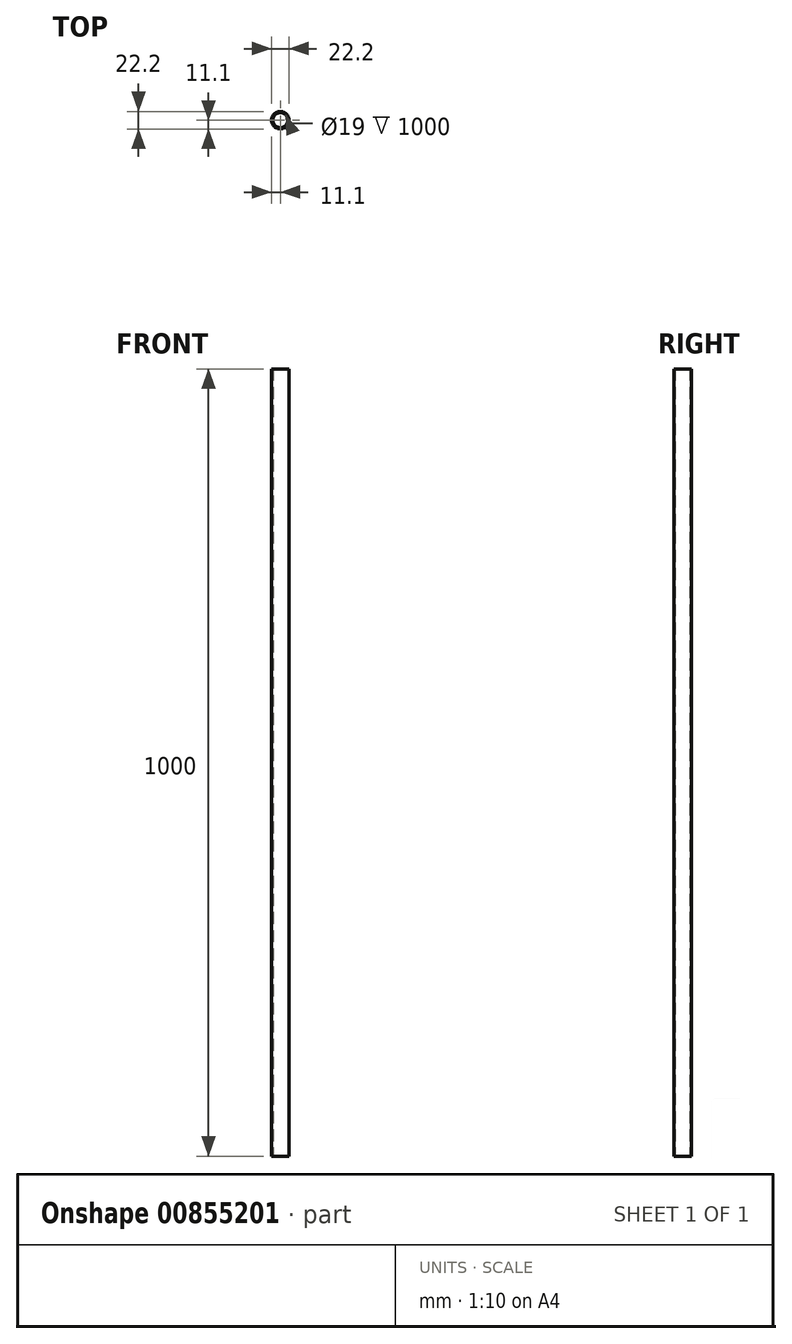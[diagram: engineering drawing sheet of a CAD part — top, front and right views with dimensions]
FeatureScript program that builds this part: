
annotation { "Feature Type Name" : "Feature", "Feature Type Description" : "" }
export const myFeature = defineFeature(function(context is Context, id is Id, definition is map)
    precondition{}
    {
        {
            var Q0;
            Q0=qCreatedBy(makeId("Top.planeOp"),FACE);
            var sketch = newSketch(context, id + "F0", { "sketchPlane" : qUnion([Q0])});
            skCircle(sketch, "E0", {"center": v(0, 0) * mm, "radius": 11.1 * mm});
            skCircle(sketch, "E1", {"center": v(0, 0) * mm, "radius": 9.5 * mm});
            skSolve(sketch);
        }
        {
            var Q0;
            Q0 = qSketchRegion(id + "F0", true);
            extrude(context, id + "F1", {"entities" : qUnion([Q0]), "depth" : 1000 * mm, "offsetDistance" : 25 * mm});
        }
    });
